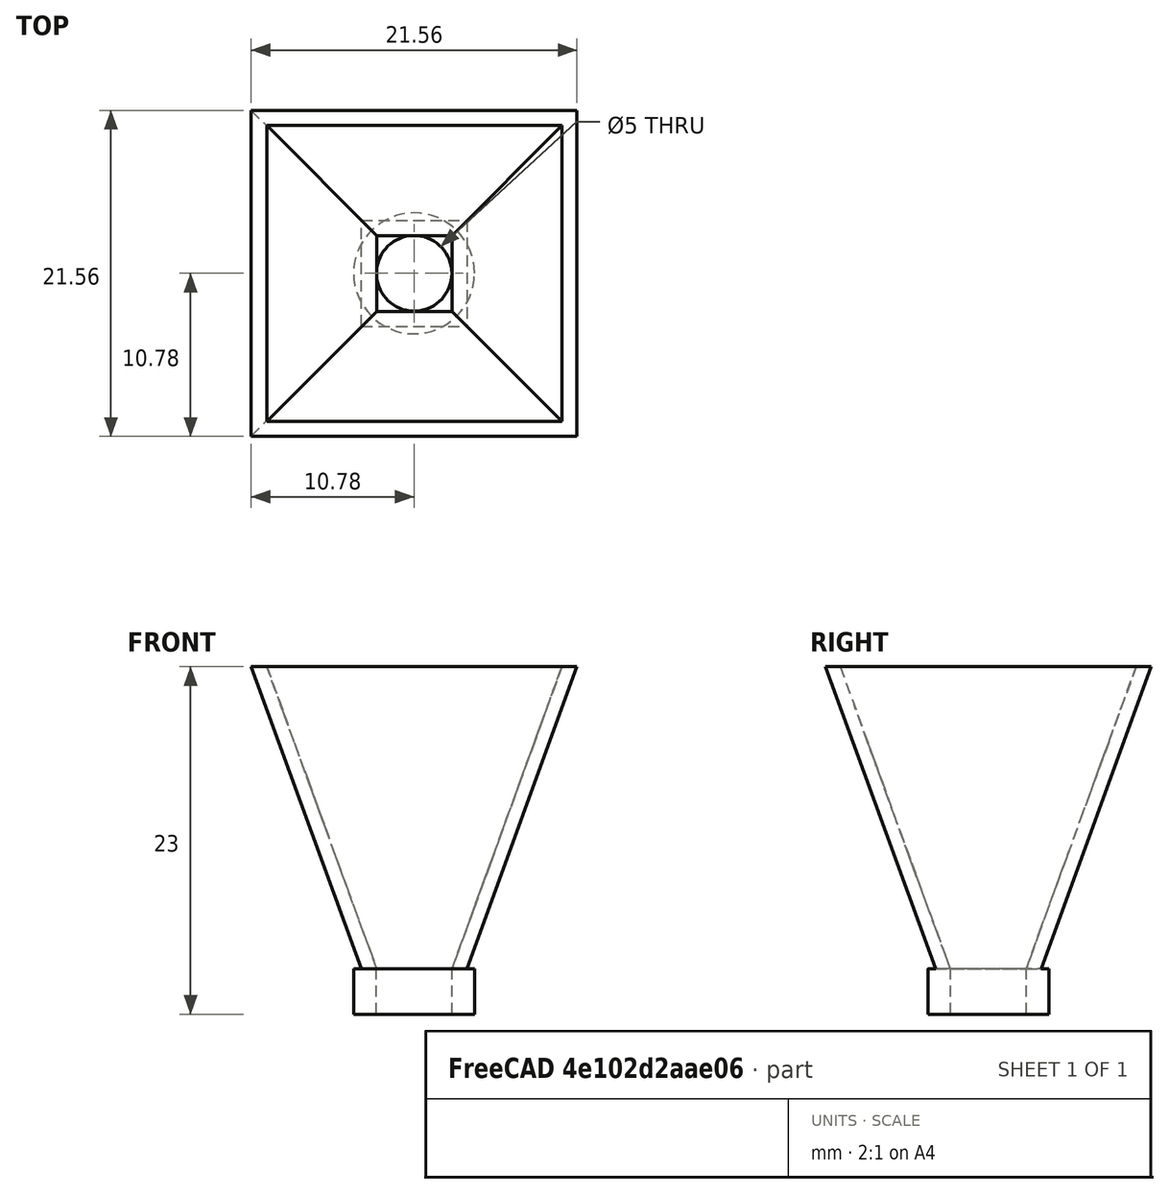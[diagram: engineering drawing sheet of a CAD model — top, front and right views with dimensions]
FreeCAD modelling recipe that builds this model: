
FCSTD DOCUMENT  (FreeCAD 0.19R24267 +99 (Git))
Label: Rectangular hopper Mice
License: All rights reserved
LicenseURL: http://en.wikipedia.org/wiki/All_rights_reserved
objects: PartDesign::FeatureBase×3, PartDesign::Body×3, Part::Feature×2, Mesh::Feature×1, Part::FeaturePython×1, Part::Compound×1
note: 10 computed .brp shape members not serialized (recipe doc carries the construction recipe); baked Part::Feature solids carry a one-line shape summary decoded from their .brp

FEATURE [Mesh::Feature] Hopper
FEATURE [Part::Feature] Hopper001
  shape: bbox 21.56 x 21.56 x 20 mm, 564 faces, 0 solids (baked)
FEATURE [Part::Feature] Hopper001_solid  label="Hopper001 (Solid)"
  shape: bbox 21.56 x 21.56 x 20 mm, 564 faces (baked)
FEATURE [Part::FeaturePython] Tube  # WARN: FeaturePython — macro-defined, semantics opaque (R4)
  AttacherType = Attacher::AttachEngine3D
  Height = 3
  InnerRadius = 2.5
  OuterRadius = 4
FEATURE [PartDesign::FeatureBase] BaseFeature
  BaseFeature = -> Tube
FEATURE [PartDesign::Body] Body
  BaseFeature = -> Tube
  Group = -> [BaseFeature]
  Origin = -> Origin
  Placement = pos=(3.5,3.5,-3) rot=(0,0,1;0rad)
  Tip = -> BaseFeature
FEATURE [PartDesign::FeatureBase] BaseFeature001
  BaseFeature = -> Hopper001_solid
FEATURE [PartDesign::Body] Body001
  BaseFeature = -> Hopper001_solid
  Group = -> [BaseFeature001]
  Origin = -> Origin001
  Tip = -> BaseFeature001
FEATURE [Part::Compound] Compound
  Links = -> [Body001,Body]
FEATURE [PartDesign::FeatureBase] BaseFeature002
  BaseFeature = -> Compound
FEATURE [PartDesign::Body] Body002
  BaseFeature = -> Compound
  Group = -> [BaseFeature002]
  Origin = -> Origin002
  Tip = -> BaseFeature002
